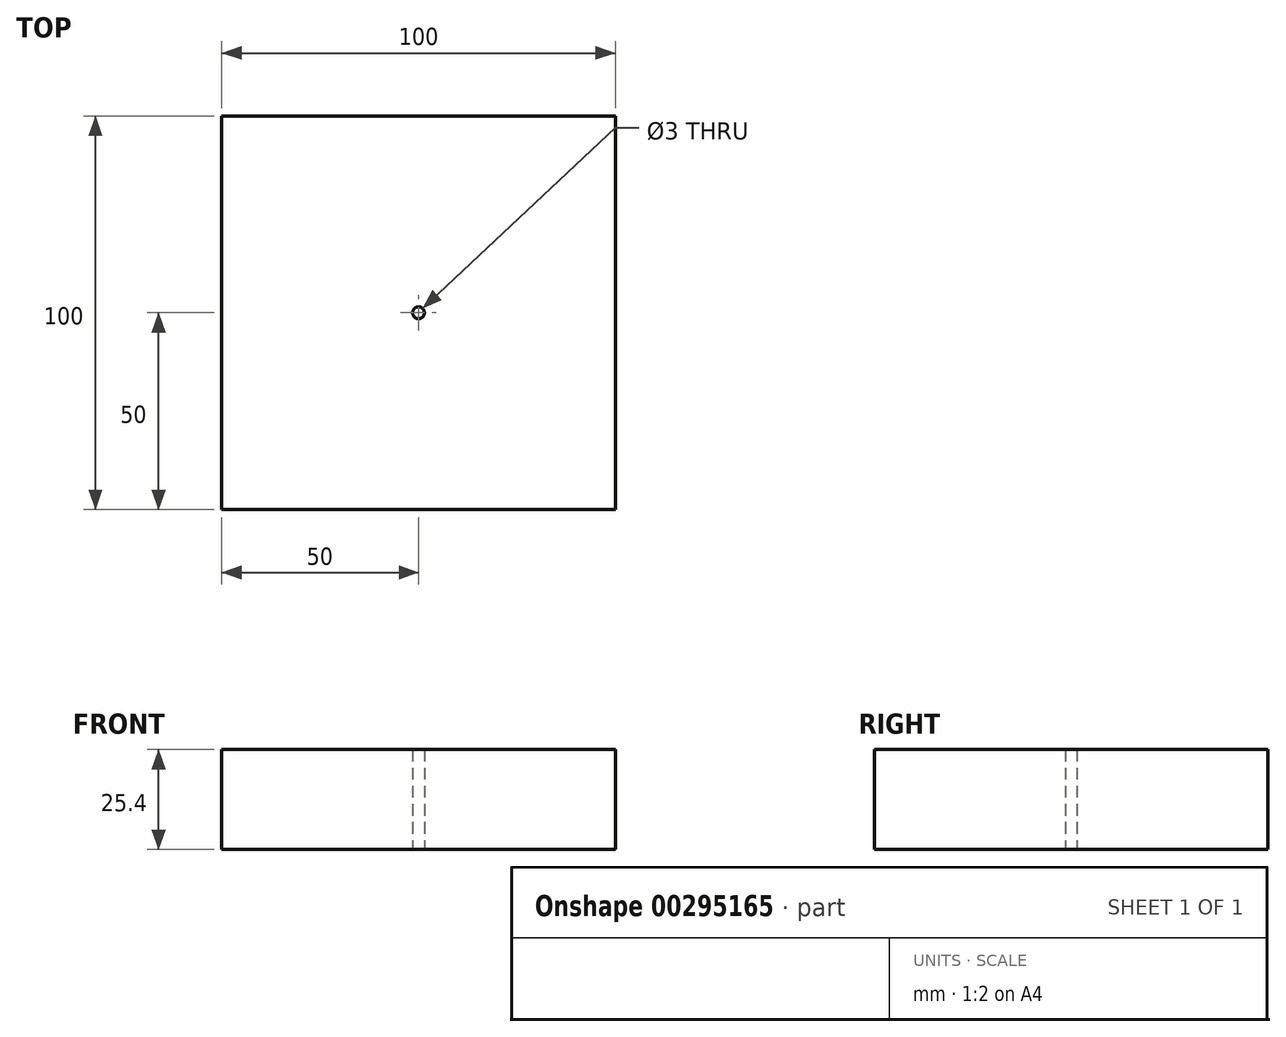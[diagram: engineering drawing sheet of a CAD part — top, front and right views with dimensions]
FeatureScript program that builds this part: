
annotation { "Feature Type Name" : "Feature", "Feature Type Description" : "" }
export const myFeature = defineFeature(function(context is Context, id is Id, definition is map)
    precondition{}
    {
        {
            var Q0;
            Q0=qCreatedBy(makeId("Top.planeOp"),FACE);
            var sketch = newSketch(context, id + "F0", { "sketchPlane" : qUnion([Q0])});
            skLineSegment(sketch, "E0.bottom", {"start": v(0, 0) * mm, "end": v(100, 0) * mm});
            skLineSegment(sketch, "E0.top", {"start": v(0, 100) * mm, "end": v(100, 100) * mm});
            skLineSegment(sketch, "E0.left", {"start": v(0, 0) * mm, "end": v(0, 100) * mm});
            skLineSegment(sketch, "E0.right", {"start": v(100, 0) * mm, "end": v(100, 100) * mm});
            skCircle(sketch, "E1", {"center": v(50, 50) * mm, "radius": 1.5 * mm});
            skPoint(sketch, "E1.centerSnap0", {"position": v(0, 50) * mm});
            skPoint(sketch, "E1.centerSnap1", {"position": v(50, 100) * mm});
            skSolve(sketch);
        }
        {
            var Q0;
            Q0=makeQuery(id+"F0.imprint","IMPRINT",FACE,{"disambiguationData":[TD([[makeQuery(id+"F0.imprint","IMPRINT",EDGE,{"derivedFrom":sQuery(id+"F0.wireOp",EDGE,"E0.bottom")}),1.0]])]});
            extrude(context, id + "F1", {"entities" : qUnion([Q0]), "depth" : 25.4 * mm});
        }
    });
